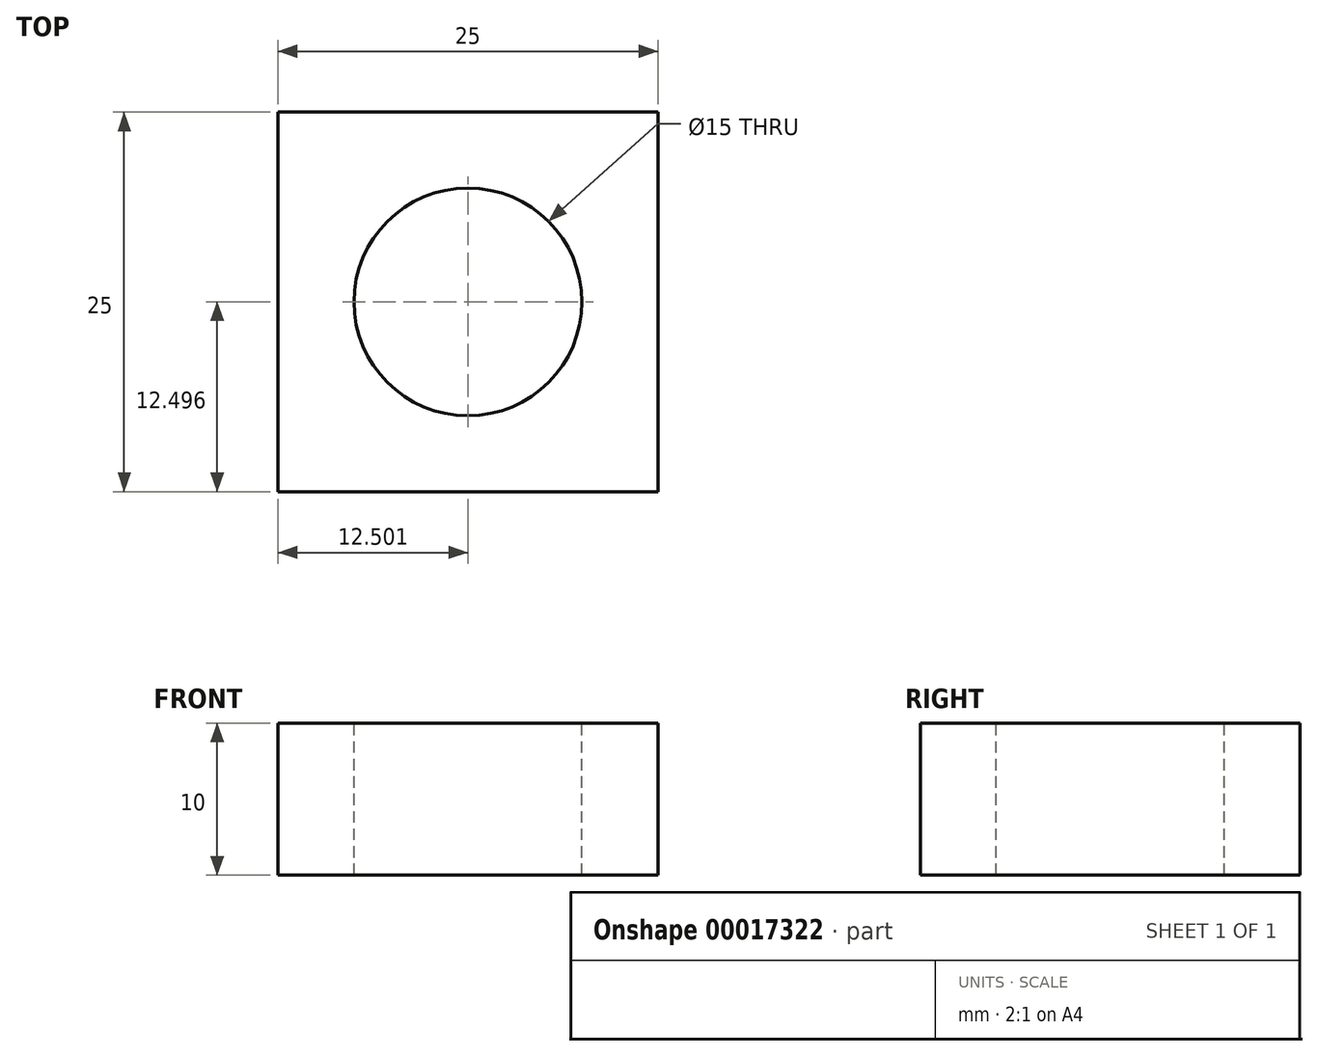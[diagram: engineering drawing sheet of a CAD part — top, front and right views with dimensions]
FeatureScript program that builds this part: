
annotation { "Feature Type Name" : "Feature", "Feature Type Description" : "" }
export const myFeature = defineFeature(function(context is Context, id is Id, definition is map)
    precondition{}
    {
        {
            var Q0;
            Q0=qCreatedBy(makeId("Top.planeOp"),FACE);
            var sketch = newSketch(context, id + "F0", { "sketchPlane" : qUnion([Q0])});
            skLineSegment(sketch, "E0.bottom", {"start": v(-13.1, 19.3) * mm, "end": v(11.9, 19.3) * mm});
            skLineSegment(sketch, "E0.top", {"start": v(-13.1, -5.7) * mm, "end": v(11.9, -5.7) * mm});
            skLineSegment(sketch, "E0.left", {"start": v(-13.1, 19.3) * mm, "end": v(-13.1, -5.7) * mm});
            skLineSegment(sketch, "E0.right", {"start": v(11.9, 19.3) * mm, "end": v(11.9, -5.7) * mm});
            skSolve(sketch);
        }
        {
            var Q0;
            Q0=makeQuery(id+"F0.imprint","IMPRINT",FACE,{"disambiguationData":[TD([[makeQuery(id+"F0.imprint","IMPRINT",EDGE,{"derivedFrom":sQuery(id+"F0.wireOp",EDGE,"E0.bottom")}),-1.0]])]});
            extrude(context, id + "F1", {"entities" : qUnion([Q0]), "oppositeDirection" : true, "depth" : 10 * mm});
        }
        {
            var Q0;
            Q0=makeQuery(id+"F1.opExtrude","CAP_FACE",FACE,{"disambiguationData":[OSD([sQuery(id+"F0.wireOp",EDGE,"E0.bottom"),sQuery(id+"F0.wireOp",EDGE,"E0.top"),sQuery(id+"F0.wireOp",EDGE,"E0.left"),sQuery(id+"F0.wireOp",EDGE,"E0.right")])],"isStart":true});
            var sketch = newSketch(context, id + "F2", { "sketchPlane" : qUnion([Q0])});
            skPoint(sketch, "E1", {"position": v(-0.6, 6.8) * mm});
            skSolve(sketch);
        }
        {
            var Q0;
            Q0=sQuery(id+"F2.wireOp",VERTEX,"E1");
            var Q1;
            Q1=makeQuery(id+"F1.opExtrude","SWEPT_BODY",BODY,{"disambiguationData":[OSD([sQuery(id+"F0.wireOp",EDGE,"E0.bottom"),sQuery(id+"F0.wireOp",EDGE,"E0.top"),sQuery(id+"F0.wireOp",EDGE,"E0.left"),sQuery(id+"F0.wireOp",EDGE,"E0.right")])]});
            hole(context, id + "F3", {"style" : HoleStyle.SIMPLE, "holeDiameter" : 15 * mm, "endStyle" : HoleEndStyle.THROUGH, "locations" : qUnion([Q0]), "scope" : qUnion([Q1])});
        }
    });
